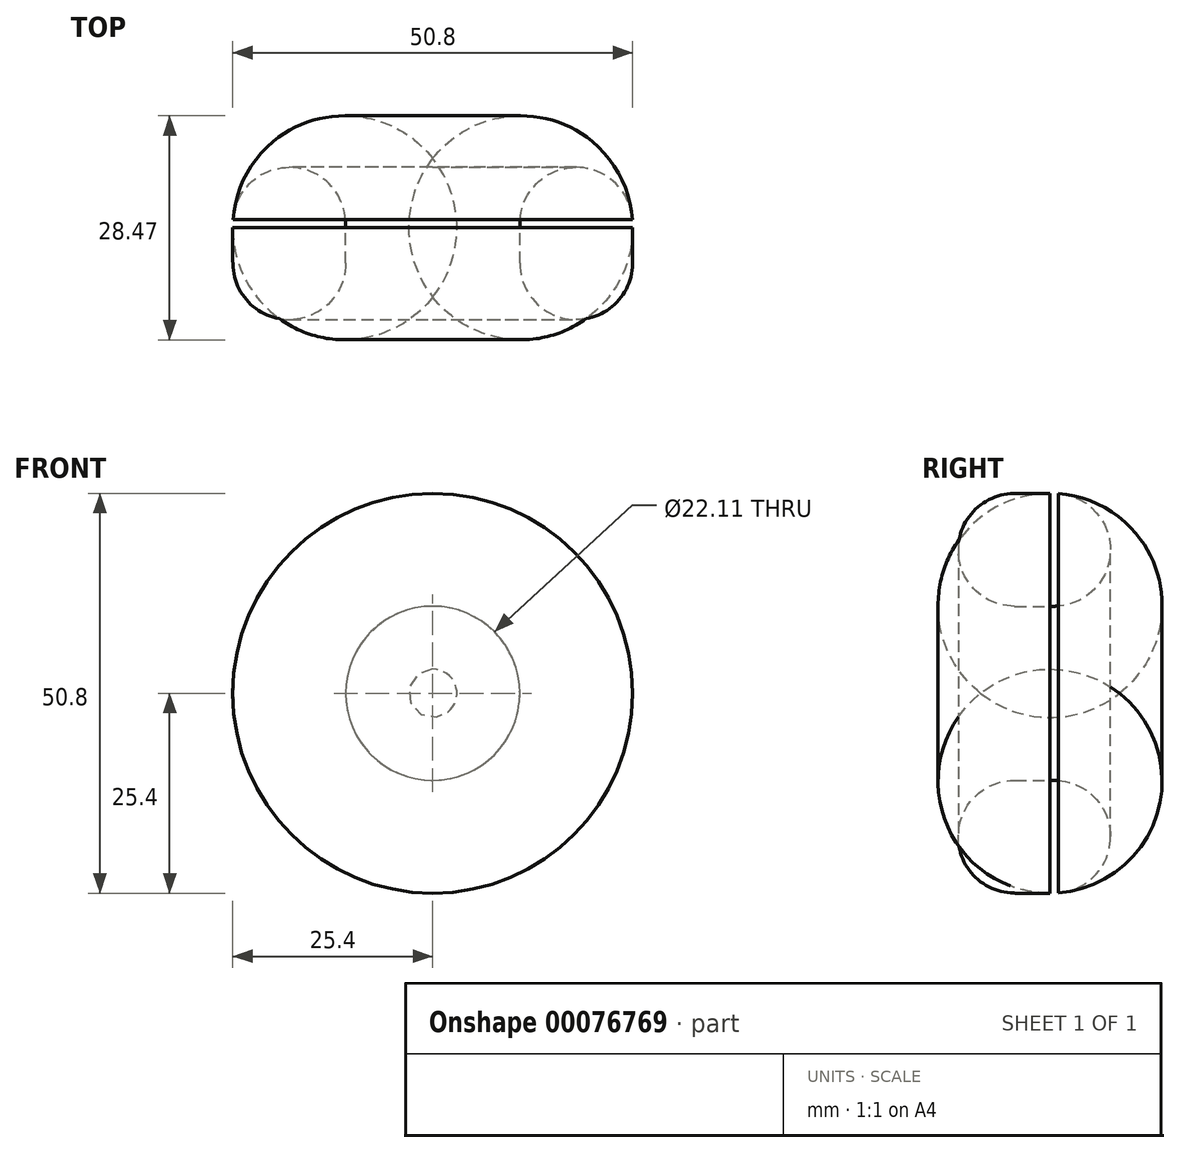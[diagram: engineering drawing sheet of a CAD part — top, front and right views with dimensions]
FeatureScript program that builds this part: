
annotation { "Feature Type Name" : "Feature", "Feature Type Description" : "" }
export const myFeature = defineFeature(function(context is Context, id is Id, definition is map)
    precondition{}
    {
        {
            var Q0;
            Q0=qCreatedBy(makeId("Front.planeOp"),FACE);
            var sketch = newSketch(context, id + "F0", { "sketchPlane" : qUnion([Q0])});
            skCircle(sketch, "E0", {"center": v(0, 0) * mm, "radius": 25.4 * mm});
            skSolve(sketch);
        }
        {
            var Q0;
            Q0 = qSketchRegion(id + "F0", true);
            extrude(context, id + "F1", {"entities" : qUnion([Q0]), "depth" : 32.46 * mm});
        }
        {
            var Q0;
            Q0=makeQuery(id+"F1.opExtrude","CAP_FACE",FACE,{"disambiguationData":[OSD([sQuery(id+"F0.wireOp",EDGE,"E0")])],"isStart":false});
            var Q1;
            Q1=makeQuery(id+"F1.opExtrude","CAP_FACE",FACE,{"disambiguationData":[OSD([sQuery(id+"F0.wireOp",EDGE,"E0")])],"isStart":true});
            fillet(context, id + "F2", {"entities" : qUnion([Q0, Q1]), "radius" : 14.23 * mm, "tangentPropagation" : true, "allowEdgeOverflow" : false});
        }
        {
            var Q0;
            Q0=qCreatedBy(makeId("Front.planeOp"),FACE);
            var sketch = newSketch(context, id + "F3", { "sketchPlane" : qUnion([Q0])});
            skCircle(sketch, "E1", {"center": v(0, 0) * mm, "radius": 11.06 * mm});
            skLineSegment(sketch, "E2", {"start": v(-11.06, 0) * mm, "end": v(0, 0) * mm, "construction": true});
            skLineSegment(sketch, "E3", {"start": v(0, 0) * mm, "end": v(11.06, 0) * mm, "construction": true});
            skLineSegment(sketch, "E4", {"start": v(0, 11.06) * mm, "end": v(0, 0) * mm, "construction": true});
            skLineSegment(sketch, "E5", {"start": v(0, -11.06) * mm, "end": v(0, 0) * mm, "construction": true});
            skSolve(sketch);
        }
        {
            var Q0;
            Q0=makeQuery(id+"F3.imprint","IMPRINT",FACE,{"disambiguationData":[TD([[makeQuery(id+"F3.imprint","IMPRINT",EDGE,{"derivedFrom":sQuery(id+"F3.wireOp",EDGE,"E1")}),1.0]])]});
            extrude(context, id + "F4", {"entities" : qUnion([Q0]), "operationType" : NewBodyOperationType.REMOVE, "depth" : 97.05 * mm});
        }
        {
            var Q0;
            Q0=makeQuery(id+"F4.boolean.opBoolean","COPY",FACE,{"derivedFrom":makeQuery(id+"F4.opExtrude","SWEPT_FACE",FACE,{"disambiguationData":[OSD([sQuery(id+"F3.wireOp",EDGE,"E1")])]})});
            fillet(context, id + "F5", {"entities" : qUnion([Q0]), "radius" : 7.16 * mm, "tangentPropagation" : true, "allowEdgeOverflow" : false});
        }
    });
